# Revit family: Winkel 40-5 3-Loch K, zn
name_source: partatom
category: HLS-Bauteile
revit_build: Autodesk Revit 2017 (Build: 20190507_1515(x64)
units: mm (PartAtom-declared; Revit-internal decimal feet)

## family parameters
Arbeitsebenenbasiert = Ja
Beim Laden mit Abzugskörper schneiden = Nein
Bemaßung runder Anschluss = Durchmesser verwenden
Gemeinsam genutzt = Ja
Immer vertikal = Nein
Raumberechnungspunkt = Nein
Teiletyp = Normal

## types (1)
- Winkel 40-5 3-Loch K, zn
    Artikelnummer = 08140400/zn
    B = 40 mm  [stored 0.131234 ft]
    Breite Material = 40 mm
    EAN = 4250928456663
    Fabrikat = MEFA
    Gewicht = 0.20 kg
    Gewicht pro Bauteil = 0.20 kg
    Kurztext1 = Winkel 3-Loch K C-Profil 45
    Kurztext2 = 90 ° Schenkel 102,5 mm 45 mm ZnNi
    L1 = 103 mm
    L2 = 45 mm  [stored 0.147638 ft]
    Lochabstand 1 = 0 mm  [stored 0 ft]
    Lochabstand 2 = 0 mm  [stored 0 ft]
    Lochdurchmesser = 13 mm
    Länge = 0 mm  [stored 0 ft]
    Material = Stahl
    Materialname = S235
    Mengeneinheit = St
    Oberflaeche = Zink-Nickel
    S = 5 mm  [stored 0.0164042 ft]
    Stärke Material = 5 mm  [stored 0.0164042 ft]
    Vorgabe-Ansicht = 1219 mm
    vpe = 50 St

note: [stored X ft] marks values corroborated as IEEE doubles in the binary element streams (Revit-internal decimal feet)
